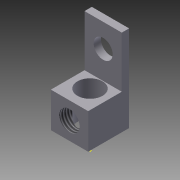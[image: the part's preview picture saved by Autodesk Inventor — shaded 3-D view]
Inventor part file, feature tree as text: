
AUTODESK INVENTOR PART (.ipt)
format: ipt  version: 2013 (Build 170138000, 138)  size: 130,048 bytes
history: native  units: mm (DEFAULTED — no unit token found)
features: other x6, sketch x4, extrude x2, hole x2, plane x2
ambient origin geometry x8: Origin, YZ Plane, XZ Plane, XY Plane, X Axis, Y Axis, Z Axis, Center Point
bodies: Solid1 (feature_tree)
feature tree (16):
  extrude  "Extrusion1"  Depth=14.0mm
  extrude  "Extrusion2"  Depth=7.0mm
  hole  "Hole1"  [1 undecoded]
  hole  "Hole2"  [1 undecoded]
  other  "Work Point1"
  other  "Work Point2"
  other  "Work Point3"
  sketch  "Sketch1"  dims[d0=12.75mm d1=14.0mm]
  sketch  "Sketch2"  dims[d2=6.375mm d3=7.0mm]
  sketch  "Sketch3"  dims[d4=12.0mm d5=0.0mm d7=2.5mm]
  sketch  "Sketch4"  dims[d8=17.5mm d9=0.0mm d10=8.0mm d11=6.375mm d12=6.5mm d13=6.0mm d14=4.0mm d15=2.0mm d16=14.3117mm d17=8.0mm d18=20.594885mm d19=6.375mm d20=6.0mm d21=6.917mm d22=6.0mm d23=4.0mm d24=2.0mm d25=14.3117mm d26=7.0mm d27=20.594885mm d28=3.175mm d29=6.35mm]
  other  "Work Axis1"
  plane  "Work Plane1"
  other  "Work Axis2"
  plane  "Work Plane2"
  other  "Work Axis3"
note: 2 required parameter values undecoded (feature->parameter linkage not recoverable at this tier; creation-order binding heuristic only, values carry confidence <= 0.55)
